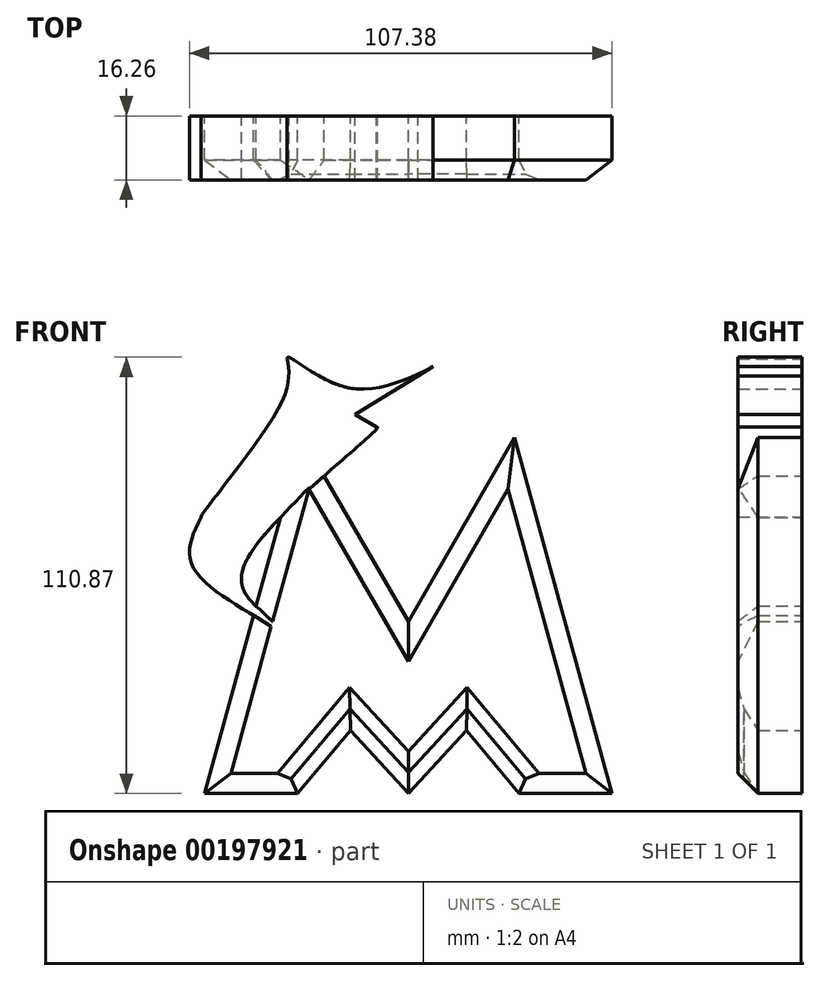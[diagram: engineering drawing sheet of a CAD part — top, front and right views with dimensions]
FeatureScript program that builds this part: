
annotation { "Feature Type Name" : "Feature", "Feature Type Description" : "" }
export const myFeature = defineFeature(function(context is Context, id is Id, definition is map)
    precondition{}
    {
        {
            var Q0;
            Q0=qCreatedBy(makeId("Front.planeOp"),FACE);
            var sketch = newSketch(context, id + "F0", { "sketchPlane" : qUnion([Q0])});
            skLineSegment(sketch, "E0.0", {"start": v(-28.13, -34.2) * mm, "end": v(-51.75, -34.2) * mm});
            skLineSegment(sketch, "E0.1", {"start": v(-14.71, -18.22) * mm, "end": v(-28.13, -34.2) * mm});
            skLineSegment(sketch, "E0.2", {"start": v(-51.75, -34.2) * mm, "end": v(-32.51, 35.89) * mm});
            skLineSegment(sketch, "E0.5", {"start": v(28.13, -34.2) * mm, "end": v(14.71, -18.22) * mm});
            skLineSegment(sketch, "E0.6", {"start": v(-21.37, 46.45) * mm, "end": v(0, 9.43) * mm});
            skLineSegment(sketch, "E0.7", {"start": v(0, 9.43) * mm, "end": v(26.96, 56.13) * mm});
            skLineSegment(sketch, "E0.8", {"start": v(26.96, 56.13) * mm, "end": v(51.75, -34.2) * mm});
            skLineSegment(sketch, "E0.9", {"start": v(51.75, -34.2) * mm, "end": v(28.13, -34.2) * mm});
            skPoint(sketch, "E1.end.orphan", {"position": v(-25.4, 44) * mm});
            skPoint(sketch, "E2.end.orphan", {"position": v(-30.32, -29.49) * mm});
            skPoint(sketch, "E3.end.orphan", {"position": v(-14, -10.03) * mm});
            skPoint(sketch, "E4.end.orphan", {"position": v(0, -34.28) * mm});
            skPoint(sketch, "E4.start.orphan", {"position": v(14, -10.03) * mm});
            skPoint(sketch, "E5.end.orphan", {"position": v(45.56, -29.49) * mm});
            skPoint(sketch, "E6.end.orphan", {"position": v(25.4, 44) * mm});
            skLineSegment(sketch, "E7", {"start": v(-0.07, -34.2) * mm, "end": v(0.07, -34.2) * mm});
            skLineSegment(sketch, "E8", {"start": v(0, -34.28) * mm, "end": v(-14.71, -18.22) * mm});
            skLineSegment(sketch, "E9", {"start": v(0, -34.28) * mm, "end": v(14.71, -18.22) * mm});
            skPoint(sketch, "E10.end.orphan", {"position": v(20.44, 73.55) * mm});
            skFitSpline(sketch, "E11", {"points": [v(-35.94, 14.74) * mm, v(-46.88, 20.97) * mm, v(-46.73, 20.21) * mm], "startDerivative": vector(-19.43, 12.42) * mm, "endDerivative": vector(2.2, -4.98) * mm});
            skFitSpline(sketch, "E12", {"points": [v(-35.94, 14.74) * mm, v(-35.94, 13.07) * mm, v(-35.94, 12.61) * mm], "startDerivative": vector(0, -2.94) * mm, "endDerivative": vector(0, -1.12) * mm});
            skPoint(sketch, "E13.0.internal.snap0", {"position": v(-39.35, 10.96) * mm});
            skFitSpline(sketch, "E13", {"points": [v(-35.94, 10.96) * mm, v(-41.56, 24.01) * mm, v(-7.83, 58.66) * mm, v(-8.13, 58.81) * mm], "startDerivative": vector(-37.48, 30.5) * mm, "endDerivative": vector(-9.71, 0.27) * mm});
            skLineSegment(sketch, "E14", {"start": v(-13.6, 62) * mm, "end": v(-7.83, 58.66) * mm});
            skLineSegment(sketch, "E15", {"start": v(-13.6, 62) * mm, "end": v(2.5, 71.73) * mm});
            skLineSegment(sketch, "E16", {"start": v(2.5, 71.73) * mm, "end": v(6.3, 74.16) * mm});
            skFitSpline(sketch, "E17", {"points": [v(6.3, 74.16) * mm, v(-16.64, 69.14) * mm, v(-30.62, 76.6) * mm, v(-30.77, 76.13) * mm], "startDerivative": vector(-44.55, -21.36) * mm, "endDerivative": vector(0.27, -8.75) * mm});
            skFitSpline(sketch, "E18", {"points": [v(-30.77, 76.13) * mm, v(-32.6, 64.43) * mm, v(-52.66, 36.02) * mm, v(-52.66, 35.86) * mm, v(-52.8, 35.86) * mm], "startDerivative": vector(4.55, -26.81) * mm, "endDerivative": vector(-5.34, 0.54) * mm});
            skFitSpline(sketch, "E19", {"points": [v(-52.66, 36.02) * mm, v(-55.24, 24.47) * mm, v(-39.35, 10.96) * mm], "startDerivative": vector(-13.29, -27.57) * mm, "endDerivative": vector(37.51, -22.77) * mm});
            skPoint(sketch, "E20.0.internal.orphan", {"position": v(-39.35, 53.87) * mm});
            skPoint(sketch, "E21.orphan", {"position": v(-26.96, 56.13) * mm});
            skSolve(sketch);
        }
        {
            var Q0;
            Q0 = qSketchRegion(id + "F0", true);
            var Q1;
            Q1=makeQuery(id+"F0.imprint","IMPRINT",FACE,{"disambiguationData":[TD([[makeQuery(id+"F0.imprint","IMPRINT",EDGE,{"derivedFrom":sQuery(id+"F0.wireOp",EDGE,"37b3371e-820a-4e14-9881-7a467c984026.0")}),-1.0]])]});
            extrude(context, id + "F1", {"entities" : qUnion([Q0, Q1]), "depth" : 16.26 * mm});
        }
        {
            var Q0;
            Q0 = qSketchRegion(id + "F0", true);
            extrude(context, id + "F2", {"entities" : qUnion([Q0]), "operationType" : NewBodyOperationType.ADD, "depth" : 8.64 * mm});
        }
        {
            var Q0;
            Q0=makeQuery(id+"F1.opExtrude","CAP_EDGE",EDGE,{"disambiguationData":[OSD([sQuery(id+"F0.wireOp",EDGE,"E0.8")])],"isStart":false});
            var Q1;
            Q1=makeQuery(id+"F1.opExtrude","CAP_EDGE",EDGE,{"disambiguationData":[OSD([sQuery(id+"F0.wireOp",EDGE,"E0.7")])],"isStart":false});
            var Q2;
            Q2=makeQuery(id+"F1.opExtrude","CAP_EDGE",EDGE,{"disambiguationData":[OSD([sQuery(id+"F0.wireOp",EDGE,"E0.6")])],"isStart":false});
            var Q3;
            Q3=makeQuery(id+"F1.opExtrude","CAP_EDGE",EDGE,{"disambiguationData":[OSD([sQuery(id+"F0.wireOp",EDGE,"E0.2")])],"isStart":false});
            var Q4;
            Q4=makeQuery(id+"F1.opExtrude","CAP_EDGE",EDGE,{"disambiguationData":[OSD([sQuery(id+"F0.wireOp",EDGE,"E0.0")])],"isStart":false});
            chamfer(context, id + "F3", {"entities" : qUnion([Q0, Q1, Q2, Q3, Q4]), "width" : 5.08 * mm, "tangentPropagation" : true});
        }
        {
            var Q0;
            Q0=makeQuery(id+"F1.opExtrude","CAP_EDGE",EDGE,{"disambiguationData":[OSD([sQuery(id+"F0.wireOp",EDGE,"E0.1")])],"isStart":false});
            var Q1;
            Q1=makeQuery(id+"F1.opExtrude","CAP_EDGE",EDGE,{"disambiguationData":[OSD([sQuery(id+"F0.wireOp",EDGE,"E8")])],"isStart":false});
            var Q2;
            Q2=makeQuery(id+"F1.opExtrude","CAP_EDGE",EDGE,{"disambiguationData":[OSD([sQuery(id+"F0.wireOp",EDGE,"E9")])],"isStart":false});
            var Q3;
            Q3=makeQuery(id+"F1.opExtrude","CAP_EDGE",EDGE,{"disambiguationData":[OSD([sQuery(id+"F0.wireOp",EDGE,"E0.5")])],"isStart":false});
            var Q4;
            Q4=makeQuery(id+"F1.opExtrude","CAP_EDGE",EDGE,{"disambiguationData":[OSD([sQuery(id+"F0.wireOp",EDGE,"E0.9")])],"isStart":false});
            chamfer(context, id + "F4", {"entities" : qUnion([Q0, Q1, Q2, Q3, Q4]), "width" : 5.08 * mm, "tangentPropagation" : true});
        }
        {
            var Q0;
            {var subQ0=sQuery(id+"F0.wireOp",EDGE,"E8");Q0=makeQuery(id+"F4.opChamfer","BLEND_EDGE",EDGE,{"blendedFrom":[makeQuery(id+"F1.opExtrude","CAP_EDGE",EDGE,{"disambiguationData":[OSD([subQ0])],"isStart":false}),makeQuery(id+"F1.opExtrude","CAP_FACE",FACE,{"disambiguationData":[OSD([sQuery(id+"F0.wireOp",EDGE,"E0.0"),sQuery(id+"F0.wireOp",EDGE,"E0.1"),sQuery(id+"F0.wireOp",EDGE,"E0.2"),sQuery(id+"F0.wireOp",EDGE,"E0.5"),sQuery(id+"F0.wireOp",EDGE,"E0.6"),sQuery(id+"F0.wireOp",EDGE,"E0.7"),sQuery(id+"F0.wireOp",EDGE,"E0.8"),sQuery(id+"F0.wireOp",EDGE,"E0.9"),subQ0,sQuery(id+"F0.wireOp",EDGE,"E9")])],"isStart":false})],"blendedInto":[makeQuery(id+"F1.opExtrude","CAP_FACE",FACE,{"disambiguationData":[OSD([sQuery(id+"F0.wireOp",EDGE,"E0.0"),sQuery(id+"F0.wireOp",EDGE,"E0.1"),sQuery(id+"F0.wireOp",EDGE,"E0.2"),sQuery(id+"F0.wireOp",EDGE,"E0.5"),sQuery(id+"F0.wireOp",EDGE,"E0.6"),sQuery(id+"F0.wireOp",EDGE,"E0.7"),sQuery(id+"F0.wireOp",EDGE,"E0.8"),sQuery(id+"F0.wireOp",EDGE,"E0.9"),subQ0,sQuery(id+"F0.wireOp",EDGE,"E9")])],"isStart":false})]});}
            var Q1;
            {var subQ0=sQuery(id+"F0.wireOp",EDGE,"E9");Q1=makeQuery(id+"F4.opChamfer","BLEND_EDGE",EDGE,{"blendedFrom":[makeQuery(id+"F1.opExtrude","CAP_EDGE",EDGE,{"disambiguationData":[OSD([subQ0])],"isStart":false}),makeQuery(id+"F1.opExtrude","CAP_FACE",FACE,{"disambiguationData":[OSD([sQuery(id+"F0.wireOp",EDGE,"E0.0"),sQuery(id+"F0.wireOp",EDGE,"E0.1"),sQuery(id+"F0.wireOp",EDGE,"E0.2"),sQuery(id+"F0.wireOp",EDGE,"E0.5"),sQuery(id+"F0.wireOp",EDGE,"E0.6"),sQuery(id+"F0.wireOp",EDGE,"E0.7"),sQuery(id+"F0.wireOp",EDGE,"E0.8"),sQuery(id+"F0.wireOp",EDGE,"E0.9"),sQuery(id+"F0.wireOp",EDGE,"E8"),subQ0])],"isStart":false})],"blendedInto":[makeQuery(id+"F1.opExtrude","CAP_FACE",FACE,{"disambiguationData":[OSD([sQuery(id+"F0.wireOp",EDGE,"E0.0"),sQuery(id+"F0.wireOp",EDGE,"E0.1"),sQuery(id+"F0.wireOp",EDGE,"E0.2"),sQuery(id+"F0.wireOp",EDGE,"E0.5"),sQuery(id+"F0.wireOp",EDGE,"E0.6"),sQuery(id+"F0.wireOp",EDGE,"E0.7"),sQuery(id+"F0.wireOp",EDGE,"E0.8"),sQuery(id+"F0.wireOp",EDGE,"E0.9"),sQuery(id+"F0.wireOp",EDGE,"E8"),subQ0])],"isStart":false})]});}
            var Q2;
            {var subQ0=sQuery(id+"F0.wireOp",EDGE,"E0.5");Q2=makeQuery(id+"F4.opChamfer","BLEND_EDGE",EDGE,{"blendedFrom":[makeQuery(id+"F1.opExtrude","CAP_EDGE",EDGE,{"disambiguationData":[OSD([subQ0])],"isStart":false}),makeQuery(id+"F1.opExtrude","CAP_FACE",FACE,{"disambiguationData":[OSD([sQuery(id+"F0.wireOp",EDGE,"E0.0"),sQuery(id+"F0.wireOp",EDGE,"E0.1"),sQuery(id+"F0.wireOp",EDGE,"E0.2"),subQ0,sQuery(id+"F0.wireOp",EDGE,"E0.6"),sQuery(id+"F0.wireOp",EDGE,"E0.7"),sQuery(id+"F0.wireOp",EDGE,"E0.8"),sQuery(id+"F0.wireOp",EDGE,"E0.9"),sQuery(id+"F0.wireOp",EDGE,"E8"),sQuery(id+"F0.wireOp",EDGE,"E9")])],"isStart":false})],"blendedInto":[makeQuery(id+"F1.opExtrude","CAP_FACE",FACE,{"disambiguationData":[OSD([sQuery(id+"F0.wireOp",EDGE,"E0.0"),sQuery(id+"F0.wireOp",EDGE,"E0.1"),sQuery(id+"F0.wireOp",EDGE,"E0.2"),subQ0,sQuery(id+"F0.wireOp",EDGE,"E0.6"),sQuery(id+"F0.wireOp",EDGE,"E0.7"),sQuery(id+"F0.wireOp",EDGE,"E0.8"),sQuery(id+"F0.wireOp",EDGE,"E0.9"),sQuery(id+"F0.wireOp",EDGE,"E8"),sQuery(id+"F0.wireOp",EDGE,"E9")])],"isStart":false})]});}
            var Q3;
            {var subQ0=sQuery(id+"F0.wireOp",EDGE,"E0.1");Q3=makeQuery(id+"F4.opChamfer","BLEND_EDGE",EDGE,{"blendedFrom":[makeQuery(id+"F1.opExtrude","CAP_EDGE",EDGE,{"disambiguationData":[OSD([subQ0])],"isStart":false}),makeQuery(id+"F1.opExtrude","CAP_FACE",FACE,{"disambiguationData":[OSD([sQuery(id+"F0.wireOp",EDGE,"E0.0"),subQ0,sQuery(id+"F0.wireOp",EDGE,"E0.2"),sQuery(id+"F0.wireOp",EDGE,"E0.5"),sQuery(id+"F0.wireOp",EDGE,"E0.6"),sQuery(id+"F0.wireOp",EDGE,"E0.7"),sQuery(id+"F0.wireOp",EDGE,"E0.8"),sQuery(id+"F0.wireOp",EDGE,"E0.9"),sQuery(id+"F0.wireOp",EDGE,"E8"),sQuery(id+"F0.wireOp",EDGE,"E9")])],"isStart":false})],"blendedInto":[makeQuery(id+"F1.opExtrude","CAP_FACE",FACE,{"disambiguationData":[OSD([sQuery(id+"F0.wireOp",EDGE,"E0.0"),subQ0,sQuery(id+"F0.wireOp",EDGE,"E0.2"),sQuery(id+"F0.wireOp",EDGE,"E0.5"),sQuery(id+"F0.wireOp",EDGE,"E0.6"),sQuery(id+"F0.wireOp",EDGE,"E0.7"),sQuery(id+"F0.wireOp",EDGE,"E0.8"),sQuery(id+"F0.wireOp",EDGE,"E0.9"),sQuery(id+"F0.wireOp",EDGE,"E8"),sQuery(id+"F0.wireOp",EDGE,"E9")])],"isStart":false})]});}
            chamfer(context, id + "F5", {"entities" : qUnion([Q0, Q1, Q2, Q3]), "width" : 5.08 * mm, "tangentPropagation" : true});
        }
    });
